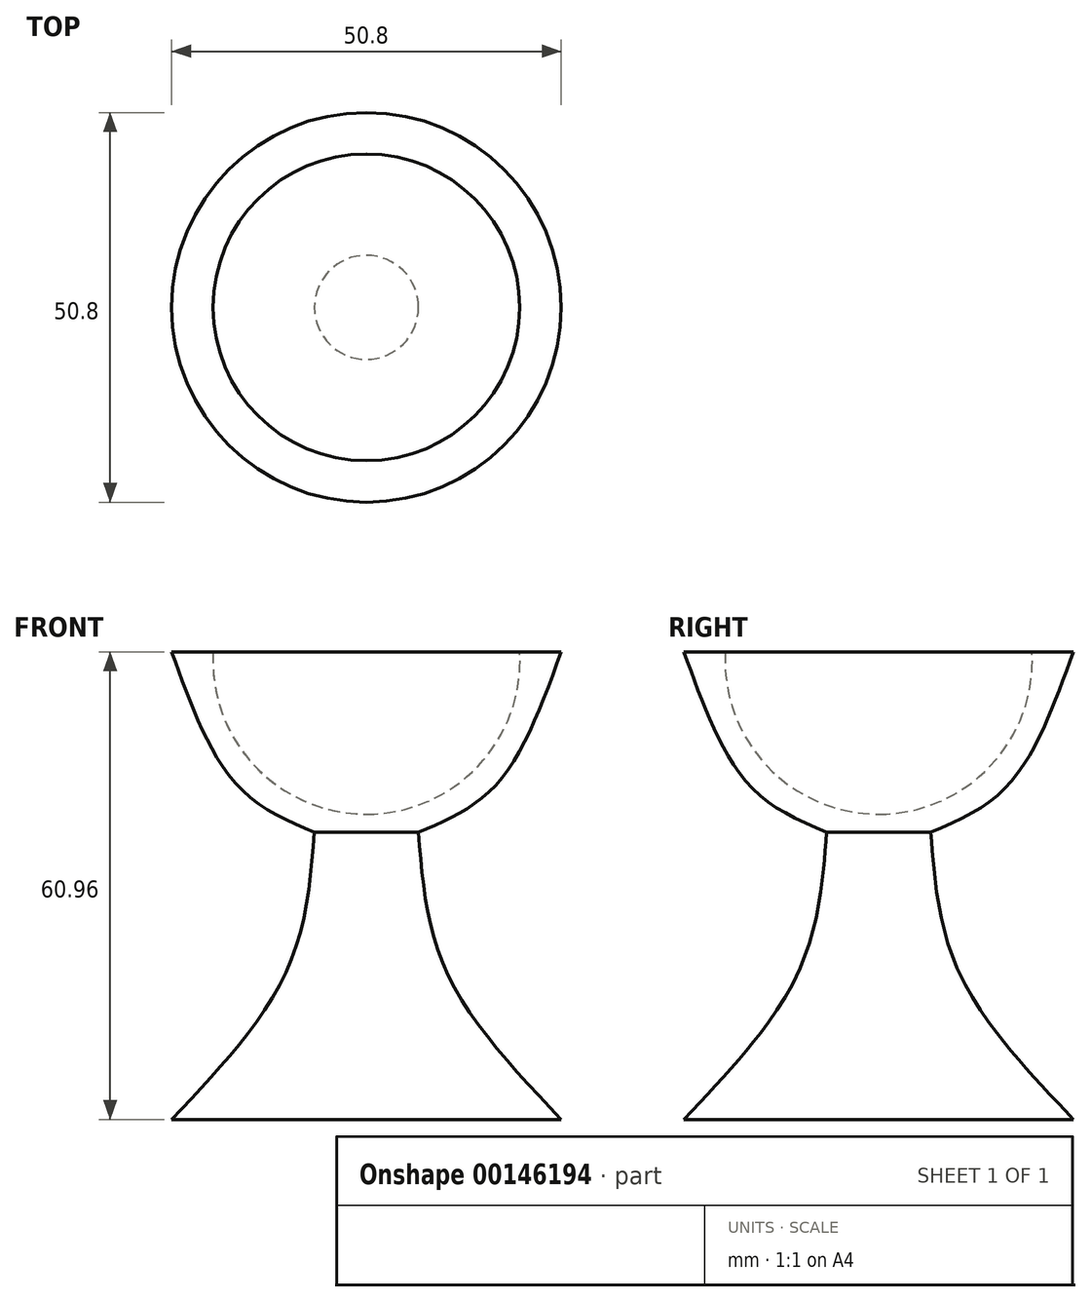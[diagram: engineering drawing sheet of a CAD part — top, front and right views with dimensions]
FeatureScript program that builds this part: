
annotation { "Feature Type Name" : "Feature", "Feature Type Description" : "" }
export const myFeature = defineFeature(function(context is Context, id is Id, definition is map)
    precondition{}
    {
        {
            var Q0;
            Q0=qCreatedBy(makeId("Top.planeOp"),FACE);
            var sketch = newSketch(context, id + "F0", { "sketchPlane" : qUnion([Q0])});
            skCircle(sketch, "E0", {"center": v(0, 0) * mm, "radius": 25.4 * mm});
            skSolve(sketch);
        }
        {
            var Q0;
            Q0 = qSketchRegion(id + "F0", true);
            extrude(context, id + "F1", {"entities" : qUnion([Q0]), "depth" : 60.96 * mm});
        }
        {
            var Q0;
            Q0=qCreatedBy(makeId("Front.planeOp"),FACE);
            var sketch = newSketch(context, id + "F2", { "sketchPlane" : qUnion([Q0])});
            skLineSegment(sketch, "E1", {"start": v(-25.4, 68.3) * mm, "end": v(-25.4, 0) * mm, "construction": true});
            skLineSegment(sketch, "E2", {"start": v(0, 68.13) * mm, "end": v(0, -16.04) * mm, "construction": true});
            skLineSegment(sketch, "E3", {"start": v(45.82, 60.96) * mm, "end": v(-47, 60.96) * mm, "construction": true});
            skLineSegment(sketch, "E4", {"start": v(-25.4, 60.96) * mm, "end": v(-25.4, 0) * mm});
            skFitSpline(sketch, "E5", {"points": [v(-25.4, 60.96) * mm, v(-16.97, 43.7) * mm, v(-6.79, 37.42) * mm], "startDerivative": vector(12.85, -35.54) * mm, "endDerivative": vector(24.85, -10.56) * mm});
            skFitSpline(sketch, "E6", {"points": [v(-6.79, 37.42) * mm, v(-10.44, 19.26) * mm, v(-25.4, 0) * mm], "startDerivative": vector(-3.15, -39.68) * mm, "endDerivative": vector(-33.38, -35.26) * mm});
            skSolve(sketch);
        }
        {
            var Q0;
            Q0 = qSketchRegion(id + "F2", true);
            var Q1;
            Q1=sQuery(id+"F2.wireOp",EDGE,"E2");
            revolve(context, id + "F3", {"operationType" : NewBodyOperationType.REMOVE, "entities" : qUnion([Q0]), "axis" : qUnion([Q1]), "revolveType" : RevolveType.FULL});
        }
        {
            var Q0;
            Q0=qCreatedBy(makeId("Front.planeOp"),FACE);
            var sketch = newSketch(context, id + "F4", { "sketchPlane" : qUnion([Q0])});
            skArc(sketch, "E7", {"start": v(0, 39.8) * mm, "mid": v(20.02, 59.82) * mm, "end": v(0, 79.84) * mm});
            skLineSegment(sketch, "E8", {"start": v(0, 79.84) * mm, "end": v(0, 39.8) * mm});
            skSolve(sketch);
        }
        {
            var Q0;
            Q0 = qSketchRegion(id + "F4", true);
            var Q1;
            Q1=sQuery(id+"F4.wireOp",EDGE,"E8");
            revolve(context, id + "F5", {"operationType" : NewBodyOperationType.REMOVE, "entities" : qUnion([Q0]), "axis" : qUnion([Q1]), "revolveType" : RevolveType.FULL, "oppositeDirection" : true});
        }
    });
